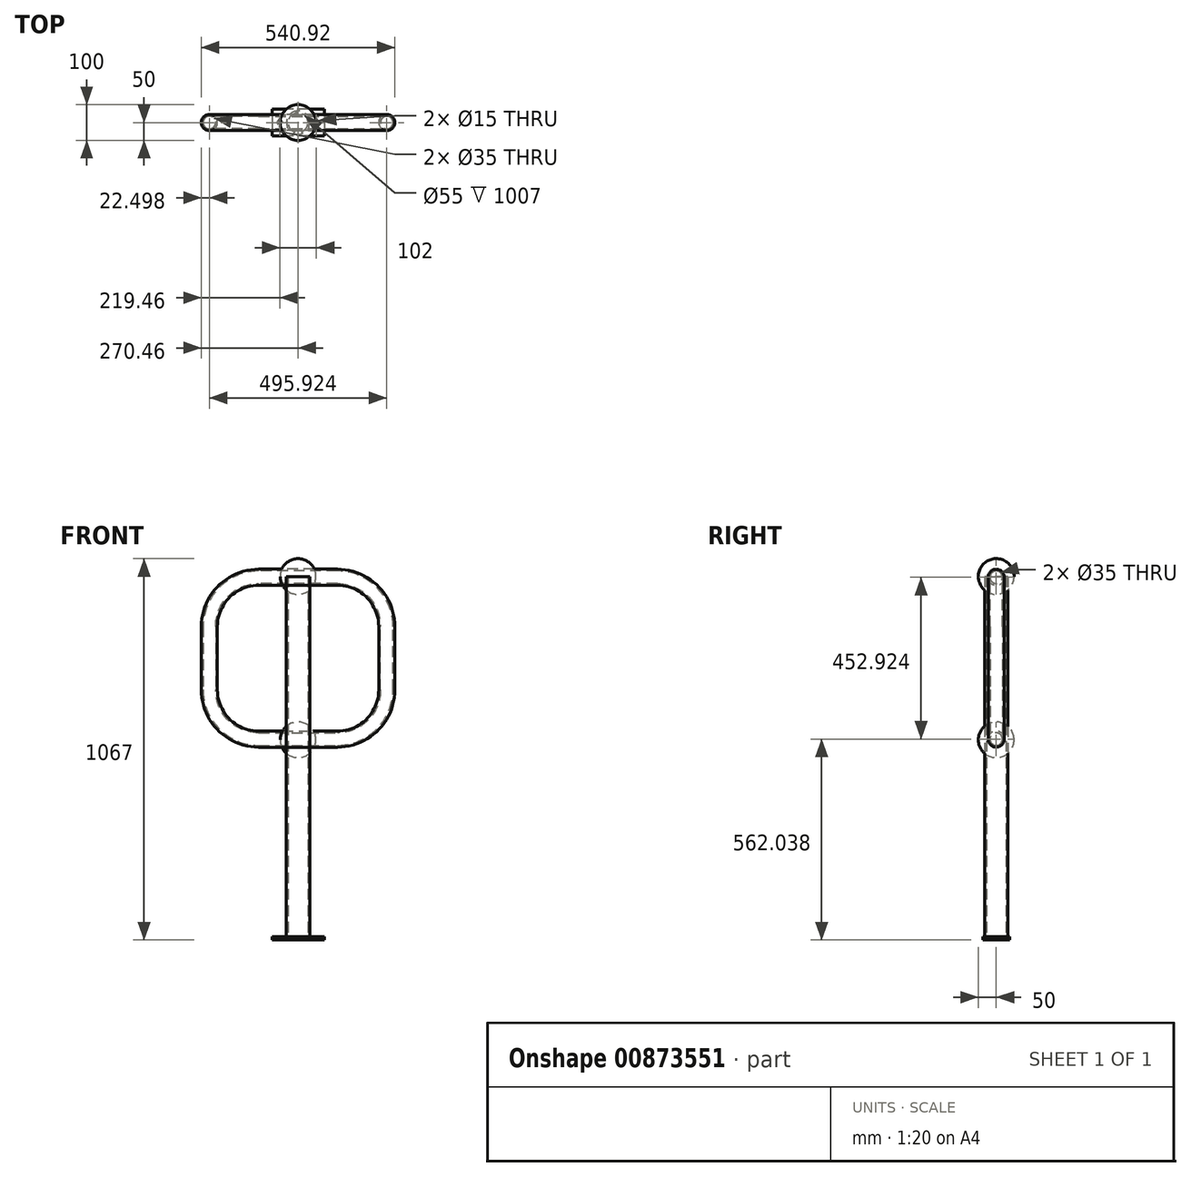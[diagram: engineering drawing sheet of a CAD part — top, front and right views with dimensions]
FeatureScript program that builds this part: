
annotation { "Feature Type Name" : "Feature", "Feature Type Description" : "" }
export const myFeature = defineFeature(function(context is Context, id is Id, definition is map)
    precondition{}
    {
        {
            var Q0;
            Q0=qCreatedBy(makeId("Front.planeOp"),FACE);
            var sketch = newSketch(context, id + "F0", { "sketchPlane" : qUnion([Q0])});
            skLineSegment(sketch, "E0", {"start": v(0, 560) * mm, "end": v(110, 560) * mm});
            skLineSegment(sketch, "E1", {"start": v(0, 0) * mm, "end": v(0, 1017) * mm, "construction": true});
            skLineSegment(sketch, "E2", {"start": v(0, 1017) * mm, "end": v(110, 1017) * mm});
            skArc(sketch, "E3", {"start": v(110, 1017) * mm, "mid": v(209, 976) * mm, "end": v(250, 877) * mm});
            skArc(sketch, "E4", {"start": v(110, 560) * mm, "mid": v(209, 601) * mm, "end": v(250, 700) * mm});
            skLineSegment(sketch, "E5", {"start": v(250, 877) * mm, "end": v(250, 700) * mm});
            skLineSegment(sketch, "E6.MirrorCS", {"start": v(-250, 877) * mm, "end": v(-250, 700) * mm});
            skArc(sketch, "E7.MirrorCS", {"start": v(-110, 1017) * mm, "mid": v(-209, 976) * mm, "end": v(-250, 877) * mm});
            skLineSegment(sketch, "E8.MirrorCS", {"start": v(0, 560) * mm, "end": v(-110, 560) * mm});
            skLineSegment(sketch, "E9.MirrorCS", {"start": v(0, 1017) * mm, "end": v(-110, 1017) * mm});
            skArc(sketch, "E10.MirrorCS", {"start": v(-110, 560) * mm, "mid": v(-209, 601) * mm, "end": v(-250, 700) * mm});
            skSolve(sketch);
        }
        {
            var Q0;
            Q0=qCreatedBy(makeId("Right.planeOp"),FACE);
            var sketch = newSketch(context, id + "F1", { "sketchPlane" : qUnion([Q0])});
            skCircle(sketch, "E11", {"center": v(0, 562.04) * mm, "radius": 22.5 * mm});
            skCircle(sketch, "E12", {"center": v(0, 562.04) * mm, "radius": 17.5 * mm});
            skSolve(sketch);
        }
        {
            var Q0;
            Q0=qSketchRegion(id+"F1",true);
            var Q1;
            Q1=qConstructionFilter(qBodyType(qCreatedBy(id+"F0",EDGE),BodyType.WIRE),ConstructionObject.NO);
            sweep(context, id + "F2", {"profiles" : qUnion([Q0]), "path" : qUnion([Q1])});
        }
        {
            var Q0;
            Q0=qCreatedBy(makeId("Top.planeOp"),FACE);
            var sketch = newSketch(context, id + "F3", { "sketchPlane" : qUnion([Q0])});
            skCircle(sketch, "E13", {"center": v(0, 0) * mm, "radius": 32.5 * mm});
            skCircle(sketch, "E14", {"center": v(0, 0) * mm, "radius": 27.5 * mm});
            skSolve(sketch);
        }
        {
            var Q0;
            Q0=qSketchRegion(id+"F3",true);
            extrude(context, id + "F4", {"entities" : qUnion([Q0]), "depth" : 1017 * mm, "offsetDistance" : 25 * mm, "hasSecondDirection" : true, "secondDirectionOppositeDirection" : false, "secondDirectionDepth" : 10 * mm});
        }
        {
            var Q0;
            {var subQ0=sQuery(id+"F3.wireOp",EDGE,"E13");var subQ1=sQuery(id+"F3.wireOp",EDGE,"E14");Q0=makeQuery(id+"F4.boolean.opBoolean","SPLIT",FACE,{"disambiguationData":[TD([makeQuery(id+"F2.opSweep","SWEPT_FACE",FACE,{"disambiguationData":[OSD([sQuery(id+"F0.wireOp",EDGE,"E2"),sQuery(id+"F1.wireOp",EDGE,"E11")])]}),makeQuery(id+"F4.opExtrude","SWEPT_FACE",FACE,{"disambiguationData":[OSD([subQ0])]}),makeQuery(id+"F4.opExtrude","SWEPT_FACE",FACE,{"disambiguationData":[OSD([subQ1])]})]),OD(0.0)],"derivedFrom":makeQuery(id+"F4.opExtrude","CAP_FACE",FACE,{"disambiguationData":[OSD([subQ0,subQ1])],"isStart":false})});}
            var sketch = newSketch(context, id + "F5", { "sketchPlane" : qUnion([Q0])});
            skArc(sketch, "E15", {"start": v(-50, 0) * mm, "mid": v(0, -50) * mm, "end": v(50, 0) * mm});
            skLineSegment(sketch, "E16", {"start": v(-50, 0) * mm, "end": v(50, 0) * mm});
            skSolve(sketch);
        }
        {
            var Q0;
            Q0=qSketchRegion(id+"F5",true);
            var Q1;
            Q1=sQuery(id+"F5.wireOp",EDGE,"E16");
            revolve(context, id + "F6", {"surfaceOperationType" : NewSurfaceOperationType.NEW, "entities" : qUnion([Q0]), "axis" : qUnion([Q1]), "revolveType" : RevolveType.FULL});
        }
        {
            var Q0;
            Q0=qCreatedBy(makeId("Top.planeOp"),FACE);
            cPlane(context, id + "F7", {"entities" : qUnion([Q0]), "cplaneType" : CPlaneType.OFFSET, "offset" : 788.5 * mm, "width" : 150 * mm, "height" : 150 * mm});
        }
        {
            var Q0;
            Q0=makeQuery(id+"F6.opRevolve","SWEPT_BODY",BODY,{"disambiguationData":[OSD([sQuery(id+"F5.wireOp",EDGE,"E15"),sQuery(id+"F5.wireOp",EDGE,"5bN2gnFG-oceZ-eyp5-UDG8-bVJ6CN20HeSy")])]});
            var Q1;
            Q1=qCreatedBy(id+"F7.planeOp",FACE);
            mirror(context, id + "F8", {"entities" : qUnion([Q0]), "mirrorPlane" : qUnion([Q1])});
        }
        {
            var Q0;
            Q0=qCreatedBy(makeId("Top.planeOp"),FACE);
            var sketch = newSketch(context, id + "F9", { "sketchPlane" : qUnion([Q0])});
            skLineSegment(sketch, "E17.bottom", {"start": v(73, 37.5) * mm, "end": v(-73, 37.5) * mm});
            skLineSegment(sketch, "E17.top", {"start": v(73, -37.5) * mm, "end": v(-73, -37.5) * mm});
            skLineSegment(sketch, "E17.left", {"start": v(73, 37.5) * mm, "end": v(73, -37.5) * mm});
            skLineSegment(sketch, "E17.right", {"start": v(-73, 37.5) * mm, "end": v(-73, -37.5) * mm});
            skPoint(sketch, "E17.middle", {"position": v(0, 0) * mm});
            skCircle(sketch, "E18", {"center": v(-51, 0) * mm, "radius": 7.5 * mm});
            skCircle(sketch, "E19.MirrorC", {"center": v(51, 0) * mm, "radius": 7.5 * mm});
            skSolve(sketch);
        }
        {
            var Q0;
            Q0=qSketchRegion(id+"F9",true);
            extrude(context, id + "F10", {"entities" : qUnion([Q0]), "depth" : 10 * mm, "offsetDistance" : 25 * mm});
        }
    });
